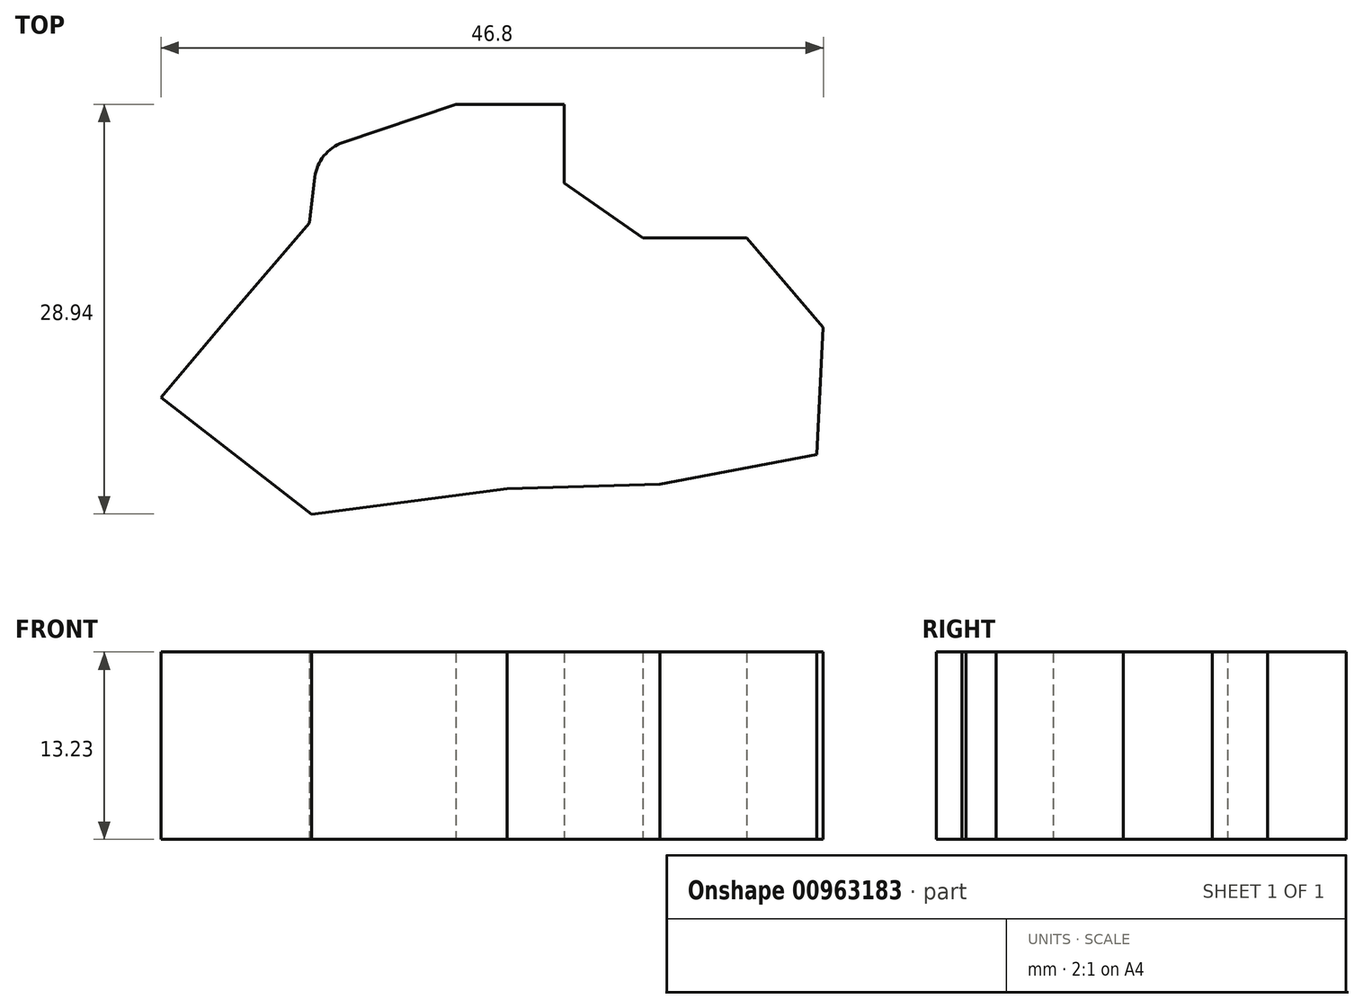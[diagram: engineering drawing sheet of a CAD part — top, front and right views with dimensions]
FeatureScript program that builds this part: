
annotation { "Feature Type Name" : "Feature", "Feature Type Description" : "" }
export const myFeature = defineFeature(function(context is Context, id is Id, definition is map)
    precondition{}
    {
        {
            var Q0;
            Q0=qCreatedBy(makeId("Top.planeOp"),FACE);
            var sketch = newSketch(context, id + "F0", { "sketchPlane" : qUnion([Q0])});
            skLineSegment(sketch, "E0", {"start": v(0, 63.3) * mm, "end": v(7.65, 63.3) * mm});
            skLineSegment(sketch, "E1", {"start": v(7.65, 63.3) * mm, "end": v(7.65, 57.74) * mm});
            skLineSegment(sketch, "E2", {"start": v(7.65, 57.74) * mm, "end": v(13.2, 53.84) * mm});
            skLineSegment(sketch, "E3", {"start": v(13.2, 53.84) * mm, "end": v(20.55, 53.84) * mm});
            skLineSegment(sketch, "E4", {"start": v(20.55, 53.84) * mm, "end": v(25.95, 47.54) * mm});
            skLineSegment(sketch, "E5", {"start": v(25.95, 47.54) * mm, "end": v(25.5, 38.54) * mm});
            skLineSegment(sketch, "E6", {"start": v(25.5, 38.54) * mm, "end": v(14.4, 36.45) * mm});
            skLineSegment(sketch, "E7", {"start": v(14.4, 36.45) * mm, "end": v(3.6, 36.15) * mm});
            skLineSegment(sketch, "E8", {"start": v(3.6, 36.15) * mm, "end": v(-10.2, 34.35) * mm});
            skLineSegment(sketch, "E9", {"start": v(-10.2, 34.35) * mm, "end": v(-20.85, 42.6) * mm});
            skLineSegment(sketch, "E10", {"start": v(-20.85, 42.6) * mm, "end": v(-15.9, 48.44) * mm});
            skLineSegment(sketch, "E11", {"start": v(-15.9, 48.44) * mm, "end": v(-10.35, 54.9) * mm});
            skLineSegment(sketch, "E12", {"start": v(-10.35, 54.9) * mm, "end": v(-9.75, 60) * mm});
            skLineSegment(sketch, "E13", {"start": v(-9.75, 60) * mm, "end": v(0, 63.3) * mm});
            skSolve(sketch);
        }
        {
            var Q0;
            Q0=makeQuery(id+"F0.imprint","IMPRINT",FACE,{"disambiguationData":[TD([[makeQuery(id+"F0.imprint","IMPRINT",EDGE,{"derivedFrom":sQuery(id+"F0.wireOp",EDGE,"E0")}),-1.0]])]});
            extrude(context, id + "F1", {"entities" : qUnion([Q0]), "depth" : 13.23 * mm, "offsetDistance" : 25.4 * mm});
        }
        {
            var Q0;
            Q0=makeQuery(id+"F1.opExtrude","SWEPT_EDGE",EDGE,{"disambiguationData":[OSD([sQuery(id+"F0.wireOp",EDGE,"E12"),sQuery(id+"F0.wireOp",EDGE,"E13")])]});
            fillet(context, id + "F2", {"entities" : qUnion([Q0]), "radius" : 2.94 * mm, "tangentPropagation" : true, "allowEdgeOverflow" : false});
        }
    });
